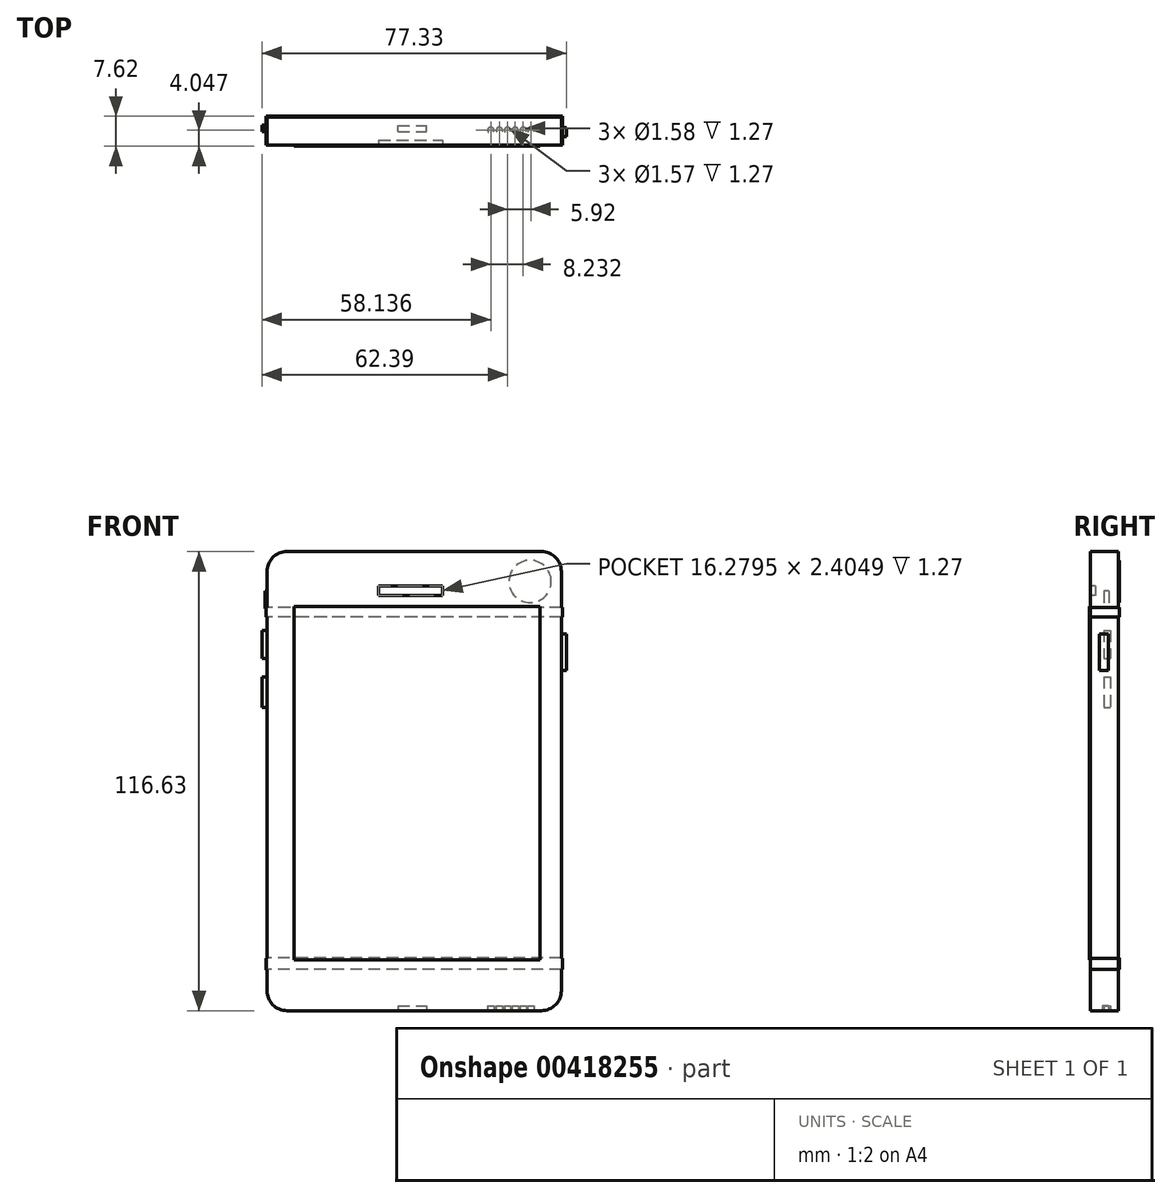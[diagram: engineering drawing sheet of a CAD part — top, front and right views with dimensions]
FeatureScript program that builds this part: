
annotation { "Feature Type Name" : "Feature", "Feature Type Description" : "" }
export const myFeature = defineFeature(function(context is Context, id is Id, definition is map)
    precondition{}
    {
        {
            var Q0;
            Q0=qCreatedBy(makeId("Front.planeOp"),FACE);
            var sketch = newSketch(context, id + "F0", { "sketchPlane" : qUnion([Q0])});
            skLineSegment(sketch, "E0.bottom", {"start": v(-36.68, 51.15) * mm, "end": v(38.11, 51.15) * mm});
            skLineSegment(sketch, "E0.top", {"start": v(-36.68, -65.48) * mm, "end": v(38.11, -65.48) * mm});
            skLineSegment(sketch, "E0.left", {"start": v(-36.68, 51.15) * mm, "end": v(-36.68, -65.48) * mm});
            skLineSegment(sketch, "E0.right", {"start": v(38.11, 51.15) * mm, "end": v(38.11, -65.48) * mm});
            skSolve(sketch);
        }
        {
            var Q0;
            Q0=makeQuery(id+"F0.imprint","IMPRINT",FACE,{"disambiguationData":[TD([[makeQuery(id+"F0.imprint","IMPRINT",EDGE,{"derivedFrom":sQuery(id+"F0.wireOp",EDGE,"E0.bottom")}),-1.0]])]});
            extrude(context, id + "F1", {"entities" : qUnion([Q0]), "depth" : 7.11 * mm});
        }
        {
            var Q0;
            Q0=makeQuery(id+"F1.opExtrude","SWEPT_FACE",FACE,{"disambiguationData":[OSD([sQuery(id+"F0.wireOp",EDGE,"E0.right")])]});
            var sketch = newSketch(context, id + "F2", { "sketchPlane" : qUnion([Q0])});
            skLineSegment(sketch, "E1.bottom", {"start": v(-4.88, 30.22) * mm, "end": v(-2.6, 30.22) * mm});
            skLineSegment(sketch, "E1.top", {"start": v(-4.88, 20.92) * mm, "end": v(-2.6, 20.92) * mm});
            skLineSegment(sketch, "E1.left", {"start": v(-4.88, 30.22) * mm, "end": v(-4.88, 20.92) * mm});
            skLineSegment(sketch, "E1.right", {"start": v(-2.6, 30.22) * mm, "end": v(-2.6, 20.92) * mm});
            skSolve(sketch);
        }
        {
            var Q0;
            Q0=makeQuery(id+"F2.imprint","IMPRINT",FACE,{"disambiguationData":[TD([[makeQuery(id+"F2.imprint","IMPRINT",EDGE,{"derivedFrom":sQuery(id+"F2.wireOp",EDGE,"E1.bottom")}),-1.0]])]});
            extrude(context, id + "F3", {"entities" : qUnion([Q0]), "operationType" : NewBodyOperationType.ADD, "depth" : 1.27 * mm});
        }
        {
            var Q0;
            Q0=makeQuery(id+"F1.opExtrude","SWEPT_FACE",FACE,{"disambiguationData":[OSD([sQuery(id+"F0.wireOp",EDGE,"E0.left")])]});
            var sketch = newSketch(context, id + "F4", { "sketchPlane" : qUnion([Q0])});
            skLineSegment(sketch, "E2.bottom", {"start": v(2.4, 41.16) * mm, "end": v(3.7, 41.16) * mm});
            skLineSegment(sketch, "E2.top", {"start": v(2.4, 36.72) * mm, "end": v(3.7, 36.72) * mm});
            skLineSegment(sketch, "E2.left", {"start": v(2.4, 41.16) * mm, "end": v(2.4, 36.72) * mm});
            skLineSegment(sketch, "E2.right", {"start": v(3.7, 41.16) * mm, "end": v(3.7, 36.72) * mm});
            skLineSegment(sketch, "E3.bottom", {"start": v(3.7, 31.17) * mm, "end": v(2.03, 31.17) * mm});
            skLineSegment(sketch, "E3.top", {"start": v(3.7, 23.96) * mm, "end": v(2.03, 23.96) * mm});
            skLineSegment(sketch, "E3.left", {"start": v(3.7, 31.17) * mm, "end": v(3.7, 23.96) * mm});
            skLineSegment(sketch, "E3.right", {"start": v(2.03, 31.17) * mm, "end": v(2.03, 23.96) * mm});
            skLineSegment(sketch, "E4.bottom", {"start": v(3.7, 19.33) * mm, "end": v(2.03, 19.33) * mm});
            skLineSegment(sketch, "E4.top", {"start": v(3.7, 11.56) * mm, "end": v(2.03, 11.56) * mm});
            skLineSegment(sketch, "E4.left", {"start": v(3.7, 19.33) * mm, "end": v(3.7, 11.56) * mm});
            skLineSegment(sketch, "E4.right", {"start": v(2.03, 19.33) * mm, "end": v(2.03, 11.56) * mm});
            skSolve(sketch);
        }
        {
            var Q0;
            Q0=makeQuery(id+"F4.imprint","IMPRINT",FACE,{"disambiguationData":[TD([[makeQuery(id+"F4.imprint","IMPRINT",EDGE,{"derivedFrom":sQuery(id+"F4.wireOp",EDGE,"E4.bottom")}),1.0]])]});
            extrude(context, id + "F5", {"entities" : qUnion([Q0]), "operationType" : NewBodyOperationType.ADD, "depth" : 1.27 * mm});
        }
        {
            var Q0;
            Q0=makeQuery(id+"F4.imprint","IMPRINT",FACE,{"disambiguationData":[TD([[makeQuery(id+"F4.imprint","IMPRINT",EDGE,{"derivedFrom":sQuery(id+"F4.wireOp",EDGE,"E3.bottom")}),1.0]])]});
            extrude(context, id + "F6", {"entities" : qUnion([Q0]), "operationType" : NewBodyOperationType.ADD, "depth" : 1.27 * mm});
        }
        {
            var Q0;
            Q0=makeQuery(id+"F4.imprint","IMPRINT",FACE,{"disambiguationData":[TD([[makeQuery(id+"F4.imprint","IMPRINT",EDGE,{"derivedFrom":sQuery(id+"F4.wireOp",EDGE,"E2.bottom")}),-1.0]])]});
            extrude(context, id + "F7", {"entities" : qUnion([Q0]), "operationType" : NewBodyOperationType.ADD, "depth" : 0.5 * mm});
        }
        {
            var Q0;
            Q0=makeQuery(id+"F1.opExtrude","SWEPT_FACE",FACE,{"disambiguationData":[OSD([sQuery(id+"F0.wireOp",EDGE,"E0.top")])]});
            var sketch = newSketch(context, id + "F8", { "sketchPlane" : qUnion([Q0])});
            skCircle(sketch, "E5", {"center": v(20.19, 3.32) * mm, "radius": 0.8 * mm});
            skCircle(sketch, "E6", {"center": v(22.36, 3.32) * mm, "radius": 0.8 * mm});
            skCircle(sketch, "E7", {"center": v(24.44, 3.32) * mm, "radius": 0.79 * mm});
            skCircle(sketch, "E8", {"center": v(26.38, 3.32) * mm, "radius": 0.79 * mm});
            skCircle(sketch, "E9", {"center": v(28.42, 3.32) * mm, "radius": 0.8 * mm});
            skCircle(sketch, "E10", {"center": v(30.36, 3.32) * mm, "radius": 0.79 * mm});
            skSolve(sketch);
        }
        {
            var Q0;
            {var subQ0=sQuery(id+"F0.wireOp",EDGE,"E0.top");Q0=makeQuery(id+"F8.imprint","IMPRINT",FACE,{"disambiguationData":[TD([[makeQuery(id+"F8.imprint","IMPRINT",EDGE,{"derivedFrom":makeQuery(id+"F1.opExtrude","CAP_EDGE",EDGE,{"disambiguationData":[OSD([subQ0])],"isStart":true})}),1.0]])]});}
            var sketch = newSketch(context, id + "F9", { "sketchPlane" : qUnion([Q0])});
            skLineSegment(sketch, "E11.bottom", {"start": v(-3.68, 3.68) * mm, "end": v(3.58, 3.68) * mm});
            skLineSegment(sketch, "E11.top", {"start": v(-3.68, 1.92) * mm, "end": v(3.58, 1.92) * mm});
            skLineSegment(sketch, "E11.left", {"start": v(-3.68, 3.68) * mm, "end": v(-3.68, 1.92) * mm});
            skLineSegment(sketch, "E11.right", {"start": v(3.58, 3.68) * mm, "end": v(3.58, 1.92) * mm});
            skSolve(sketch);
        }
        {
            var Q0;
            Q0=makeQuery(id+"F1.opExtrude","CAP_FACE",FACE,{"disambiguationData":[OSD([sQuery(id+"F0.wireOp",EDGE,"E0.bottom"),sQuery(id+"F0.wireOp",EDGE,"E0.top"),sQuery(id+"F0.wireOp",EDGE,"E0.left"),sQuery(id+"F0.wireOp",EDGE,"E0.right")])],"isStart":false});
            var sketch = newSketch(context, id + "F10", { "sketchPlane" : qUnion([Q0])});
            skLineSegment(sketch, "E12.bottom", {"start": v(-8.32, 42.46) * mm, "end": v(7.95, 42.46) * mm});
            skLineSegment(sketch, "E12.top", {"start": v(-8.32, 40.05) * mm, "end": v(7.95, 40.05) * mm});
            skLineSegment(sketch, "E12.left", {"start": v(-8.32, 42.46) * mm, "end": v(-8.32, 40.05) * mm});
            skLineSegment(sketch, "E12.right", {"start": v(7.95, 42.46) * mm, "end": v(7.95, 40.05) * mm});
            skSolve(sketch);
        }
        {
            var Q0;
            Q0=makeQuery(id+"F10.imprint","IMPRINT",FACE,{"disambiguationData":[TD([[makeQuery(id+"F10.imprint","IMPRINT",EDGE,{"derivedFrom":sQuery(id+"F10.wireOp",EDGE,"E12.bottom")}),-1.0]])]});
            extrude(context, id + "F11", {"entities" : qUnion([Q0]), "operationType" : NewBodyOperationType.REMOVE, "oppositeDirection" : true, "depth" : 1.27 * mm});
        }
        {
            var Q0;
            Q0=makeQuery(id+"F1.opExtrude","CAP_FACE",FACE,{"disambiguationData":[OSD([sQuery(id+"F0.wireOp",EDGE,"E0.bottom"),sQuery(id+"F0.wireOp",EDGE,"E0.top"),sQuery(id+"F0.wireOp",EDGE,"E0.left"),sQuery(id+"F0.wireOp",EDGE,"E0.right")])],"isStart":false});
            var sketch = newSketch(context, id + "F12", { "sketchPlane" : qUnion([Q0])});
            skCircle(sketch, "E13", {"center": v(0, -57.65) * mm, "radius": 4.2 * mm});
            skSolve(sketch);
        }
        {
            var Q0;
            Q0=sQuery(id+"F12.wireOp",EDGE,"E13");
            extrude(context, id + "F13", {"bodyType" : ToolBodyType.SURFACE, "surfaceEntities" : qUnion([Q0]), "depth" : 0.5 * mm});
        }
        {
            var Q0;
            Q0=makeQuery(id+"F1.opExtrude","SWEPT_EDGE",EDGE,{"disambiguationData":[OSD([sQuery(id+"F0.wireOp",EDGE,"E0.bottom"),sQuery(id+"F0.wireOp",EDGE,"E0.right")])]});
            fillet(context, id + "F14", {"entities" : qUnion([Q0]), "radius" : 5.08 * mm, "tangentPropagation" : true, "allowEdgeOverflow" : false});
        }
        {
            var Q0;
            Q0=makeQuery(id+"F1.opExtrude","SWEPT_EDGE",EDGE,{"disambiguationData":[OSD([sQuery(id+"F0.wireOp",EDGE,"E0.bottom"),sQuery(id+"F0.wireOp",EDGE,"E0.left")])]});
            var Q1;
            Q1=makeQuery(id+"F1.opExtrude","SWEPT_EDGE",EDGE,{"disambiguationData":[OSD([sQuery(id+"F0.wireOp",EDGE,"E0.top"),sQuery(id+"F0.wireOp",EDGE,"E0.left")])]});
            var Q2;
            Q2=makeQuery(id+"F1.opExtrude","SWEPT_EDGE",EDGE,{"disambiguationData":[OSD([sQuery(id+"F0.wireOp",EDGE,"E0.top"),sQuery(id+"F0.wireOp",EDGE,"E0.right")])]});
            fillet(context, id + "F15", {"entities" : qUnion([Q0, Q1, Q2]), "radius" : 5.08 * mm, "tangentPropagation" : true, "allowEdgeOverflow" : false});
        }
        {
            var Q0;
            Q0=makeQuery(id+"F1.opExtrude","CAP_FACE",FACE,{"disambiguationData":[OSD([sQuery(id+"F0.wireOp",EDGE,"E0.bottom"),sQuery(id+"F0.wireOp",EDGE,"E0.top"),sQuery(id+"F0.wireOp",EDGE,"E0.left"),sQuery(id+"F0.wireOp",EDGE,"E0.right")])],"isStart":false});
            var sketch = newSketch(context, id + "F16", { "sketchPlane" : qUnion([Q0])});
            skLineSegment(sketch, "E14.bottom", {"start": v(-29.77, 37.17) * mm, "end": v(32.64, 37.17) * mm});
            skLineSegment(sketch, "E14.top", {"start": v(-29.77, -52.6) * mm, "end": v(32.64, -52.6) * mm});
            skLineSegment(sketch, "E14.left", {"start": v(-29.77, 37.17) * mm, "end": v(-29.77, -52.6) * mm});
            skLineSegment(sketch, "E14.right", {"start": v(32.64, 37.17) * mm, "end": v(32.64, -52.6) * mm});
            skSolve(sketch);
        }
        {
            var Q0;
            Q0=makeQuery(id+"F16.imprint","IMPRINT",FACE,{"disambiguationData":[TD([[makeQuery(id+"F16.imprint","IMPRINT",EDGE,{"derivedFrom":sQuery(id+"F16.wireOp",EDGE,"E14.bottom")}),-1.0]])]});
            extrude(context, id + "F17", {"entities" : qUnion([Q0]), "operationType" : NewBodyOperationType.ADD, "depth" : 0.25 * mm});
        }
        {
            var Q0;
            Q0=qCreatedBy(makeId("Top.planeOp"),FACE);
            var sketch = newSketch(context, id + "F18", { "sketchPlane" : qUnion([Q0])});
            skCircle(sketch, "E15", {"center": v(-31.45, -3.24) * mm, "radius": 2.03 * mm});
            skCircle(sketch, "E16", {"center": v(-26.08, -3.24) * mm, "radius": 1.68 * mm});
            skSolve(sketch);
        }
        {
            var Q0;
            Q0=sQuery(id+"F18.wireOp",EDGE,"E16");
            extrude(context, id + "F19", {"bodyType" : ToolBodyType.SURFACE, "surfaceEntities" : qUnion([Q0]), "oppositeDirection" : true, "depth" : 65.8 * mm});
        }
        {
            var Q0;
            Q0=sQuery(id+"F18.wireOp",EDGE,"E15");
            extrude(context, id + "F20", {"bodyType" : ToolBodyType.SURFACE, "surfaceEntities" : qUnion([Q0]), "oppositeDirection" : true, "depth" : 65.53 * mm});
        }
        {
            var Q0;
            Q0=qCreatedBy(makeId("Front.planeOp"),FACE);
            var sketch = newSketch(context, id + "F21", { "sketchPlane" : qUnion([Q0])});
            skCircle(sketch, "E17", {"center": v(30.15, 43.57) * mm, "radius": 5.38 * mm});
            skCircle(sketch, "E18", {"center": v(21.64, 43.57) * mm, "radius": 1.3 * mm});
            skCircle(sketch, "E19", {"center": v(16.1, 43.57) * mm, "radius": 2.77 * mm});
            skSolve(sketch);
        }
        {
            var Q0;
            Q0=makeQuery(id+"F21.imprint","IMPRINT",FACE,{"disambiguationData":[TD([[makeQuery(id+"F21.imprint","IMPRINT",EDGE,{"derivedFrom":sQuery(id+"F21.wireOp",EDGE,"E17")}),1.0]])]});
            extrude(context, id + "F22", {"entities" : qUnion([Q0]), "operationType" : NewBodyOperationType.ADD, "oppositeDirection" : true, "depth" : 0.25 * mm});
        }
        {
            var Q0;
            Q0=sQuery(id+"F21.wireOp",EDGE,"E18");
            extrude(context, id + "F23", {"bodyType" : ToolBodyType.SURFACE, "surfaceEntities" : qUnion([Q0]), "oppositeDirection" : true, "depth" : 0.25 * mm});
        }
        {
            var Q0;
            Q0=sQuery(id+"F21.wireOp",EDGE,"E19");
            extrude(context, id + "F24", {"bodyType" : ToolBodyType.SURFACE, "surfaceEntities" : qUnion([Q0]), "oppositeDirection" : true, "depth" : 0.25 * mm});
        }
        {
            var Q0;
            Q0=makeQuery(id+"F1.opExtrude","CAP_FACE",FACE,{"disambiguationData":[OSD([sQuery(id+"F0.wireOp",EDGE,"E0.bottom"),sQuery(id+"F0.wireOp",EDGE,"E0.top"),sQuery(id+"F0.wireOp",EDGE,"E0.left"),sQuery(id+"F0.wireOp",EDGE,"E0.right")])],"isStart":true});
            var sketch = newSketch(context, id + "F25", { "sketchPlane" : qUnion([Q0])});
            skLineSegment(sketch, "E20", {"start": v(-38.11, 36.9) * mm, "end": v(36.68, 36.9) * mm});
            skLineSegment(sketch, "E21", {"start": v(-38.11, 34.5) * mm, "end": v(36.68, 34.5) * mm});
            skSolve(sketch);
        }
        {
            var Q0;
            {var subQ0=sQuery(id+"F25.wireOp",EDGE,"E20");Q0=makeQuery(id+"F25.imprint","IMPRINT",FACE,{"disambiguationData":[TD([[makeQuery(id+"F25.imprint","IMPRINT",EDGE,{"derivedFrom":subQ0}),-1.0]])]});}
            extrude(context, id + "F26", {"entities" : qUnion([Q0]), "operationType" : NewBodyOperationType.ADD, "depth" : 0.25 * mm});
        }
        {
            var Q0;
            {var subQ0=sQuery(id+"F0.wireOp",EDGE,"E0.right");Q0=makeQuery(id+"F26.boolean.opBoolean","MERGE",FACE,{"derivedFrom":[makeQuery(id+"F1.opExtrude","SWEPT_FACE",FACE,{"disambiguationData":[OSD([subQ0])]}),makeQuery(id+"F26.opExtrude","SWEPT_FACE",FACE,{"disambiguationData":[OSD([subQ0])]})]});}
            var sketch = newSketch(context, id + "F27", { "sketchPlane" : qUnion([Q0])});
            skLineSegment(sketch, "E22", {"start": v(0.25, 36.9) * mm, "end": v(-7.11, 36.9) * mm});
            skLineSegment(sketch, "E23", {"start": v(0.25, 34.5) * mm, "end": v(-7.11, 34.5) * mm});
            skSolve(sketch);
        }
        {
            var Q0;
            {var subQ0=sQuery(id+"F0.wireOp",EDGE,"E0.left");Q0=makeQuery(id+"F26.boolean.opBoolean","MERGE",FACE,{"derivedFrom":[makeQuery(id+"F1.opExtrude","SWEPT_FACE",FACE,{"disambiguationData":[OSD([subQ0])]}),makeQuery(id+"F26.opExtrude","SWEPT_FACE",FACE,{"disambiguationData":[OSD([subQ0])]})]});}
            var sketch = newSketch(context, id + "F28", { "sketchPlane" : qUnion([Q0])});
            skLineSegment(sketch, "E24", {"start": v(0, 36.9) * mm, "end": v(7.11, 36.9) * mm});
            skLineSegment(sketch, "E25", {"start": v(0, 34.5) * mm, "end": v(7.11, 34.5) * mm});
            skSolve(sketch);
        }
        {
            var Q0;
            {var subQ1=sQuery(id+"F0.wireOp",EDGE,"E0.right");var subQ2=makeQuery(id+"F26.opExtrude","CAP_EDGE",EDGE,{"disambiguationData":[OSD([subQ1])],"isStart":false});Q0=makeQuery(id+"F27.imprint","IMPRINT",FACE,{"disambiguationData":[TD([[makeQuery(id+"F27.imprint","IMPRINT",EDGE,{"derivedFrom":subQ2}),-1.0]])]});}
            extrude(context, id + "F29", {"entities" : qUnion([Q0]), "operationType" : NewBodyOperationType.ADD, "depth" : 0.25 * mm});
        }
        {
            var Q0;
            {var subQ7=sQuery(id+"F28.wireOp",EDGE,"E25");Q0=makeQuery(id+"F28.imprint","IMPRINT",FACE,{"disambiguationData":[TD([[makeQuery(id+"F28.imprint","IMPRINT",EDGE,{"derivedFrom":subQ7}),1.0]])]});}
            extrude(context, id + "F30", {"entities" : qUnion([Q0]), "operationType" : NewBodyOperationType.ADD, "depth" : 0.25 * mm});
        }
        {
            var Q0;
            {var subQ0=sQuery(id+"F0.wireOp",EDGE,"E0.left");var subQ1=sQuery(id+"F0.wireOp",EDGE,"E0.top");var subQ2=sQuery(id+"F0.wireOp",EDGE,"E0.right");Q0=makeQuery(id+"F26.boolean.opBoolean","SPLIT",FACE,{"disambiguationData":[TD([makeQuery(id+"F1.opExtrude","SWEPT_FACE",FACE,{"disambiguationData":[OSD([subQ1])]})])],"derivedFrom":makeQuery(id+"F1.opExtrude","CAP_FACE",FACE,{"disambiguationData":[OSD([sQuery(id+"F0.wireOp",EDGE,"E0.bottom"),subQ1,subQ0,subQ2])],"isStart":true})});}
            var sketch = newSketch(context, id + "F31", { "sketchPlane" : qUnion([Q0])});
            skLineSegment(sketch, "E26", {"start": v(-38.11, -52.08) * mm, "end": v(36.68, -52.08) * mm});
            skLineSegment(sketch, "E27", {"start": v(-38.11, -55.01) * mm, "end": v(36.68, -55.01) * mm});
            skSolve(sketch);
        }
        {
            var Q0;
            {var subQ0=sQuery(id+"F0.wireOp",EDGE,"E0.right");Q0=makeQuery(id+"F29.boolean.opBoolean","SPLIT",FACE,{"disambiguationData":[TD([makeQuery(id+"F3.opExtrude","SWEPT_FACE",FACE,{"disambiguationData":[OSD([sQuery(id+"F2.wireOp",EDGE,"E1.bottom")])]})])],"derivedFrom":makeQuery(id+"F26.boolean.opBoolean","MERGE",FACE,{"derivedFrom":[makeQuery(id+"F1.opExtrude","SWEPT_FACE",FACE,{"disambiguationData":[OSD([subQ0])]}),makeQuery(id+"F26.opExtrude","SWEPT_FACE",FACE,{"disambiguationData":[OSD([subQ0])]})]})});}
            var sketch = newSketch(context, id + "F32", { "sketchPlane" : qUnion([Q0])});
            skLineSegment(sketch, "E28", {"start": v(0, -54.97) * mm, "end": v(-7.11, -54.97) * mm});
            skLineSegment(sketch, "E29", {"start": v(0, -52.15) * mm, "end": v(-7.11, -52.15) * mm});
            skSolve(sketch);
        }
        {
            var Q0;
            {var subQ0=sQuery(id+"F0.wireOp",EDGE,"E0.left");Q0=makeQuery(id+"F30.boolean.opBoolean","SPLIT",FACE,{"disambiguationData":[TD([makeQuery(id+"F5.opExtrude","SWEPT_FACE",FACE,{"disambiguationData":[OSD([sQuery(id+"F4.wireOp",EDGE,"E4.bottom")])]})])],"derivedFrom":makeQuery(id+"F26.boolean.opBoolean","MERGE",FACE,{"derivedFrom":[makeQuery(id+"F1.opExtrude","SWEPT_FACE",FACE,{"disambiguationData":[OSD([subQ0])]}),makeQuery(id+"F26.opExtrude","SWEPT_FACE",FACE,{"disambiguationData":[OSD([subQ0])]})]})});}
            var sketch = newSketch(context, id + "F33", { "sketchPlane" : qUnion([Q0])});
            skLineSegment(sketch, "E30", {"start": v(0, -52.2) * mm, "end": v(7.11, -52.2) * mm});
            skLineSegment(sketch, "E31", {"start": v(0, -55.05) * mm, "end": v(7.11, -55.05) * mm});
            skSolve(sketch);
        }
        {
            var Q0;
            {var subQ0=sQuery(id+"F31.wireOp",EDGE,"E26");Q0=makeQuery(id+"F31.imprint","IMPRINT",FACE,{"disambiguationData":[TD([[makeQuery(id+"F31.imprint","IMPRINT",EDGE,{"derivedFrom":subQ0}),-1.0]])]});}
            extrude(context, id + "F34", {"entities" : qUnion([Q0]), "operationType" : NewBodyOperationType.ADD, "depth" : 0.25 * mm});
        }
        {
            var Q0;
            {var subQ0=sQuery(id+"F32.wireOp",EDGE,"E28");Q0=makeQuery(id+"F32.imprint","IMPRINT",FACE,{"disambiguationData":[TD([[makeQuery(id+"F32.imprint","IMPRINT",EDGE,{"derivedFrom":subQ0}),-1.0]])]});}
            extrude(context, id + "F35", {"entities" : qUnion([Q0]), "operationType" : NewBodyOperationType.ADD, "depth" : 0.25 * mm});
        }
        {
            var Q0;
            {var subQ0=sQuery(id+"F33.wireOp",EDGE,"E30");Q0=makeQuery(id+"F33.imprint","IMPRINT",FACE,{"disambiguationData":[TD([[makeQuery(id+"F33.imprint","IMPRINT",EDGE,{"derivedFrom":subQ0}),-1.0]])]});}
            extrude(context, id + "F36", {"entities" : qUnion([Q0]), "operationType" : NewBodyOperationType.ADD, "depth" : 0.25 * mm});
        }
        {
            var Q0;
            {var subQ0=sQuery(id+"F25.wireOp",EDGE,"E21");var subQ1=makeQuery(id+"F26.opExtrude","SWEPT_FACE",FACE,{"disambiguationData":[OSD([subQ0])]});var subQ2=sQuery(id+"F0.wireOp",EDGE,"E0.left");var subQ3=sQuery(id+"F0.wireOp",EDGE,"E0.top");var subQ4=sQuery(id+"F0.wireOp",EDGE,"E0.right");var subQ5=makeQuery(id+"F1.opExtrude","CAP_FACE",FACE,{"disambiguationData":[OSD([sQuery(id+"F0.wireOp",EDGE,"E0.bottom"),subQ3,subQ2,subQ4])],"isStart":false});var subQ6=makeQuery(id+"F1.opExtrude","CAP_EDGE",EDGE,{"disambiguationData":[OSD([subQ4])],"isStart":false});var subQ8=makeQuery(id+"F29.opExtrude","SWEPT_FACE",FACE,{"disambiguationData":[OSD([subQ4]),TDD([makeQuery(id+"F27.imprint","IMPRINT",EDGE,{"disambiguationData":[TD([[makeQuery(id+"F27.imprint","INTERSECT",VERTEX,{"derivedFrom":[subQ6,sQuery(id+"F27.wireOp",EDGE,"E22")]}),-1.0]])],"derivedFrom":subQ6})])]});var subQ11=makeQuery(id+"F1.opExtrude","CAP_EDGE",EDGE,{"disambiguationData":[OSD([subQ2])],"isStart":false});var subQ12=makeQuery(id+"F30.opExtrude","SWEPT_FACE",FACE,{"disambiguationData":[OSD([subQ2]),TDD([makeQuery(id+"F28.imprint","IMPRINT",EDGE,{"disambiguationData":[TD([[makeQuery(id+"F28.imprint","INTERSECT",VERTEX,{"derivedFrom":[subQ11,sQuery(id+"F28.wireOp",EDGE,"E24")]}),-1.0]])],"derivedFrom":subQ11})])]});var subQ13=makeQuery(id+"F30.boolean.opBoolean","SPLIT",EDGE,{"disambiguationData":[TD([subQ1])],"derivedFrom":subQ11});var subQ14=makeQuery(id+"F29.boolean.opBoolean","SPLIT",EDGE,{"disambiguationData":[TD([subQ1])],"derivedFrom":subQ6});Q0=makeQuery(id+"F36.boolean.opBoolean","MERGE",FACE,{"derivedFrom":[makeQuery(id+"F35.boolean.opBoolean","MERGE",FACE,{"derivedFrom":[makeQuery(id+"F30.boolean.opBoolean","MERGE",FACE,{"derivedFrom":[makeQuery(id+"F29.boolean.opBoolean","MERGE",FACE,{"derivedFrom":[subQ5,subQ8]}),subQ12]}),makeQuery(id+"F35.opExtrude","SWEPT_FACE",FACE,{"disambiguationData":[OSD([subQ4]),TDD([makeQuery(id+"F32.imprint","IMPRINT",EDGE,{"disambiguationData":[TD([[makeQuery(id+"F32.imprint","INTERSECT",VERTEX,{"derivedFrom":[subQ14,sQuery(id+"F32.wireOp",EDGE,"E28")]}),1.0]])],"derivedFrom":subQ14})])]})]}),makeQuery(id+"F36.opExtrude","SWEPT_FACE",FACE,{"disambiguationData":[OSD([subQ2]),TDD([makeQuery(id+"F33.imprint","IMPRINT",EDGE,{"disambiguationData":[TD([[makeQuery(id+"F33.imprint","INTERSECT",VERTEX,{"derivedFrom":[subQ13,sQuery(id+"F33.wireOp",EDGE,"E30")]}),-1.0]])],"derivedFrom":subQ13})])]})]});}
            var sketch = newSketch(context, id + "F37", { "sketchPlane" : qUnion([Q0])});
            skCircle(sketch, "E32", {"center": v(-13.69, 41.49) * mm, "radius": 0.97 * mm});
            skPoint(sketch, "E32.centerSnap0", {"position": v(-36.68, 41.49) * mm});
            skSolve(sketch);
        }
        {
            var Q0;
            Q0=sQuery(id+"F37.wireOp",EDGE,"E32");
            extrude(context, id + "F38", {"bodyType" : ToolBodyType.SURFACE, "surfaceEntities" : qUnion([Q0]), "depth" : 0.25 * mm});
        }
        {
            var Q0;
            Q0=makeQuery(id+"F8.imprint","IMPRINT",FACE,{"disambiguationData":[TD([[makeQuery(id+"F8.imprint","IMPRINT",EDGE,{"derivedFrom":sQuery(id+"F8.wireOp",EDGE,"E5")}),1.0]])]});
            var Q1;
            Q1=sQuery(id+"F8.wireOp",EDGE,"E5");
            extrude(context, id + "F39", {"entities" : qUnion([Q0]), "operationType" : NewBodyOperationType.REMOVE, "surfaceEntities" : qUnion([Q1]), "oppositeDirection" : true, "depth" : 1.27 * mm});
        }
        {
            var Q0;
            Q0=makeQuery(id+"F9.imprint","IMPRINT",FACE,{"disambiguationData":[TD([[makeQuery(id+"F9.imprint","IMPRINT",EDGE,{"derivedFrom":makeQuery(id+"F8.imprint","IMPRINT",EDGE,{"derivedFrom":sQuery(id+"F8.wireOp",EDGE,"E10")})}),1.0]])]});
            var Q1;
            Q1=makeQuery(id+"F9.imprint","IMPRINT",FACE,{"disambiguationData":[TD([[makeQuery(id+"F9.imprint","IMPRINT",EDGE,{"derivedFrom":makeQuery(id+"F8.imprint","IMPRINT",EDGE,{"derivedFrom":sQuery(id+"F8.wireOp",EDGE,"E9")})}),1.0]])]});
            var Q2;
            Q2=makeQuery(id+"F9.imprint","IMPRINT",FACE,{"disambiguationData":[TD([[makeQuery(id+"F9.imprint","IMPRINT",EDGE,{"derivedFrom":makeQuery(id+"F8.imprint","IMPRINT",EDGE,{"derivedFrom":sQuery(id+"F8.wireOp",EDGE,"E8")})}),1.0]])]});
            var Q3;
            Q3=makeQuery(id+"F9.imprint","IMPRINT",FACE,{"disambiguationData":[TD([[makeQuery(id+"F9.imprint","IMPRINT",EDGE,{"derivedFrom":makeQuery(id+"F8.imprint","IMPRINT",EDGE,{"derivedFrom":sQuery(id+"F8.wireOp",EDGE,"E7")})}),1.0]])]});
            var Q4;
            Q4=makeQuery(id+"F9.imprint","IMPRINT",FACE,{"disambiguationData":[TD([[makeQuery(id+"F9.imprint","IMPRINT",EDGE,{"derivedFrom":makeQuery(id+"F8.imprint","IMPRINT",EDGE,{"derivedFrom":sQuery(id+"F8.wireOp",EDGE,"E6")})}),1.0]])]});
            extrude(context, id + "F40", {"entities" : qUnion([Q0, Q1, Q2, Q3, Q4]), "operationType" : NewBodyOperationType.REMOVE, "oppositeDirection" : true, "depth" : 1.27 * mm});
        }
        {
            var Q0;
            Q0=makeQuery(id+"F1.opExtrude","SWEPT_FACE",FACE,{"disambiguationData":[OSD([sQuery(id+"F0.wireOp",EDGE,"E0.top")])]});
            var sketch = newSketch(context, id + "F41", { "sketchPlane" : qUnion([Q0])});
            skLineSegment(sketch, "E33.bottom", {"start": v(-3.41, 3.7) * mm, "end": v(3.91, 3.7) * mm});
            skLineSegment(sketch, "E33.top", {"start": v(-3.41, 2.07) * mm, "end": v(3.91, 2.07) * mm});
            skLineSegment(sketch, "E33.left", {"start": v(-3.41, 3.7) * mm, "end": v(-3.41, 2.07) * mm});
            skLineSegment(sketch, "E33.right", {"start": v(3.91, 3.7) * mm, "end": v(3.91, 2.07) * mm});
            skSolve(sketch);
        }
        {
            var Q0;
            Q0=makeQuery(id+"F41.imprint","IMPRINT",FACE,{"disambiguationData":[TD([[makeQuery(id+"F41.imprint","IMPRINT",EDGE,{"derivedFrom":sQuery(id+"F41.wireOp",EDGE,"E33.bottom")}),-1.0]])]});
            extrude(context, id + "F42", {"entities" : qUnion([Q0]), "operationType" : NewBodyOperationType.REMOVE, "oppositeDirection" : true, "depth" : 1.27 * mm});
        }
    });
